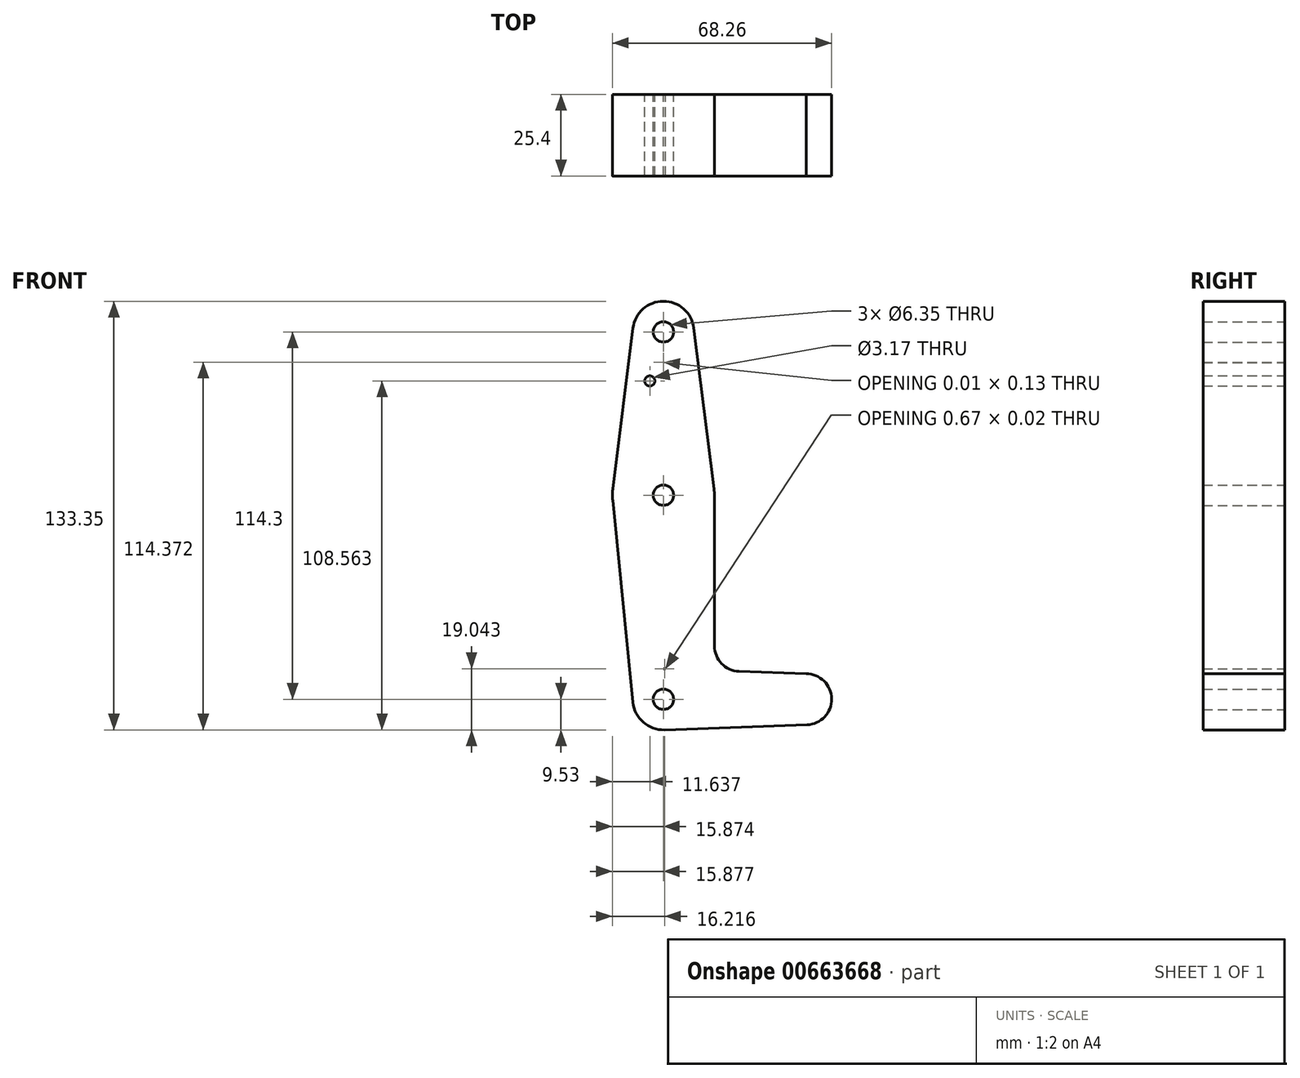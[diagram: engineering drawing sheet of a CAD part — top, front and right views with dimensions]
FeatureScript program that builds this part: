
annotation { "Feature Type Name" : "Feature", "Feature Type Description" : "" }
export const myFeature = defineFeature(function(context is Context, id is Id, definition is map)
    precondition{}
    {
        {
            var Q0;
            Q0=qCreatedBy(makeId("Front.planeOp"),FACE);
            var sketch = newSketch(context, id + "F0", { "sketchPlane" : qUnion([Q0])});
            skLineSegment(sketch, "E0", {"start": v(-44.73, 50.8) * mm, "end": v(-44.73, -63.5) * mm});
            skLineSegment(sketch, "E1", {"start": v(-44.73, -63.5) * mm, "end": v(-0.28, -63.5) * mm});
            skCircle(sketch, "E2", {"center": v(-44.73, 50.8) * mm, "radius": 9.53 * mm});
            skCircle(sketch, "E3", {"center": v(-44.73, 0) * mm, "radius": 15.88 * mm});
            skArc(sketch, "E4", {"start": v(-44.06, -54) * mm, "mid": v(-44.4, -53.98) * mm, "end": v(-44.73, -53.98) * mm});
            skLineSegment(sketch, "E5", {"start": v(-54.21, -64.45) * mm, "end": v(-60.53, -1.59) * mm});
            skLineSegment(sketch, "E6", {"start": v(-28.86, -46.87) * mm, "end": v(-28.86, 0) * mm});
            skLineSegment(sketch, "E7", {"start": v(-0.28, -55.56) * mm, "end": v(-21.2, -54.81) * mm});
            skLineSegment(sketch, "E8", {"start": v(-44.73, -53.98) * mm, "end": v(-44.06, -54) * mm});
            skLineSegment(sketch, "E9", {"start": v(-44.73, -73.02) * mm, "end": v(-44.73, -73.02) * mm});
            skLineSegment(sketch, "E10", {"start": v(-54.18, 52) * mm, "end": v(-60.48, 1.98) * mm});
            skLineSegment(sketch, "E11", {"start": v(-35.28, 52) * mm, "end": v(-28.98, 1.98) * mm});
            skCircle(sketch, "E12", {"center": v(-44.73, 0) * mm, "radius": 3.18 * mm});
            skCircle(sketch, "E13", {"center": v(-44.73, 50.8) * mm, "radius": 3.18 * mm});
            skCircle(sketch, "E14", {"center": v(-44.73, -63.5) * mm, "radius": 3.18 * mm});
            skArc(sketch, "E15.filletArc", {"start": v(-28.86, -46.87) * mm, "mid": v(-26.63, -52.39) * mm, "end": v(-21.2, -54.81) * mm});
            skPoint(sketch, "E16.orphan", {"position": v(-0.28, -73.02) * mm});
            skPoint(sketch, "E17.center.orphan", {"position": v(-0.28, -63.5) * mm});
            skLineSegment(sketch, "E18", {"start": v(-44.73, -73.03) * mm, "end": v(-44.73, -73.03) * mm});
            skPoint(sketch, "E19.orphan", {"position": v(-0.28, -73.03) * mm});
            skCircle(sketch, "E20", {"center": v(-0.28, -63.5) * mm, "radius": 7.94 * mm});
            skCircle(sketch, "E21", {"center": v(-44.73, -63.5) * mm, "radius": 9.53 * mm});
            skLineSegment(sketch, "E22", {"start": v(-44.4, -73.02) * mm, "end": v(0, -71.43) * mm});
            skArc(sketch, "E23", {"start": v(-44.74, 41.28) * mm, "mid": v(-44.73, 41.34) * mm, "end": v(-44.73, 41.4) * mm});
            skCircle(sketch, "E24", {"center": v(-48.97, 35.53) * mm, "radius": 1.59 * mm});
            skSolve(sketch);
        }
        {
            var Q0;
            Q0 = qSketchRegion(id + "F0", true);
            var Q1;
            {var subQ5=sQuery(id+"F0.wireOp",EDGE,"E8");Q1=makeQuery(id+"F0.imprint","IMPRINT",FACE,{"disambiguationData":[TD([[makeQuery(id+"F0.imprint","IMPRINT",EDGE,{"derivedFrom":subQ5}),-1.0]])]});}
            extrude(context, id + "F1", {"entities" : qUnion([Q0, Q1]), "depth" : 25.4 * mm, "offsetDistance" : 25.4 * mm});
        }
    });
